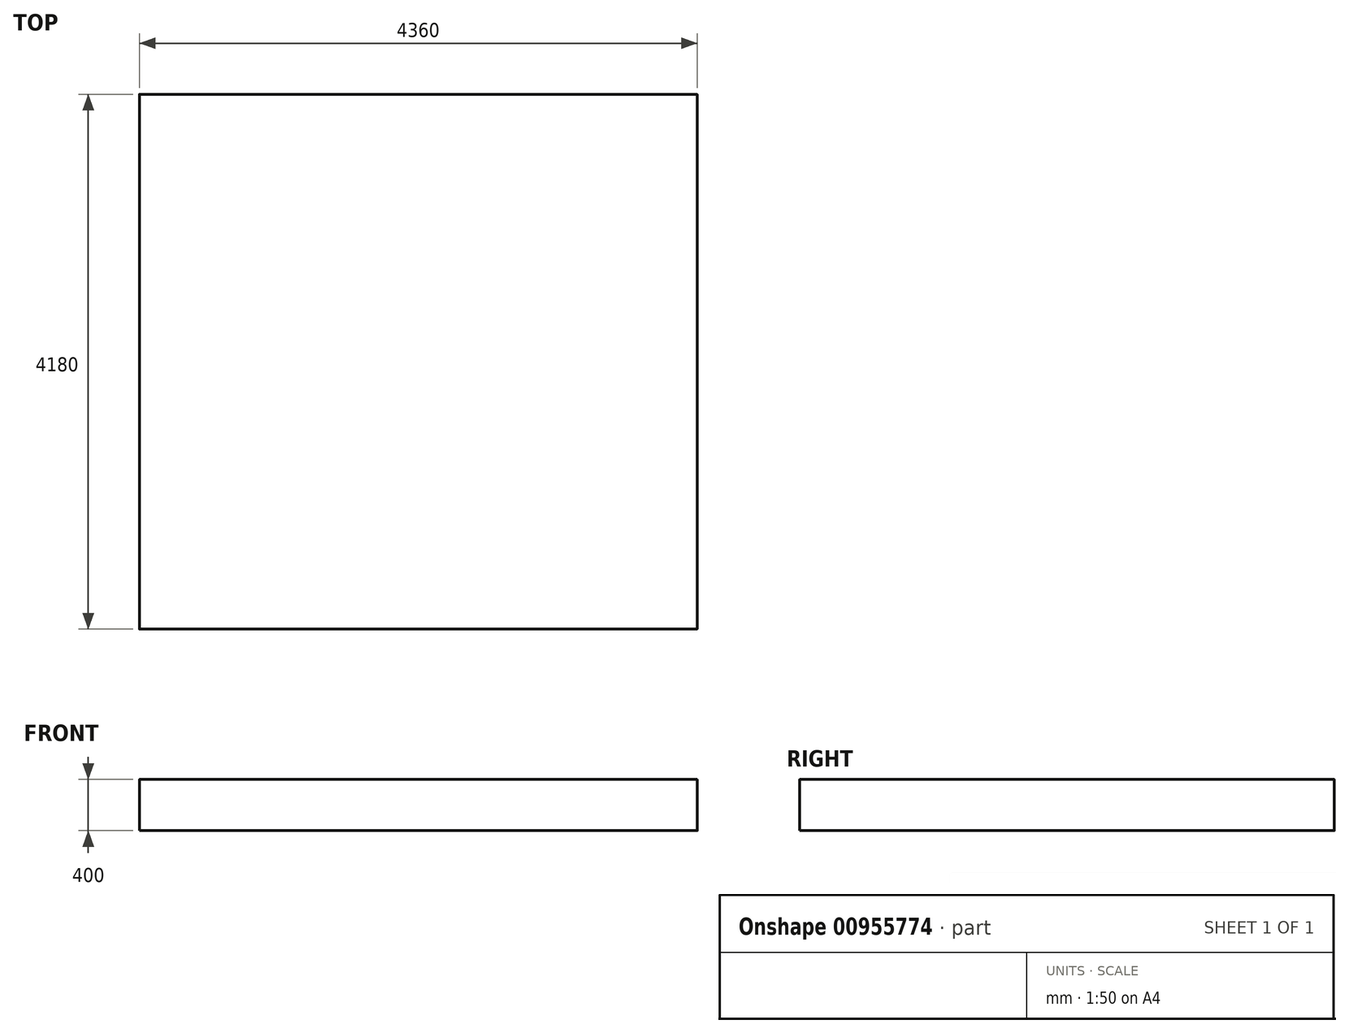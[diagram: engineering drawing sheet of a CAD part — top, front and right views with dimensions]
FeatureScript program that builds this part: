
annotation { "Feature Type Name" : "Feature", "Feature Type Description" : "" }
export const myFeature = defineFeature(function(context is Context, id is Id, definition is map)
    precondition{}
    {
        {
            var Q0;
            Q0=qCreatedBy(makeId("Top.planeOp"),FACE);
            var sketch = newSketch(context, id + "F0", { "sketchPlane" : qUnion([Q0])});
            skLineSegment(sketch, "E0.bottom", {"start": v(-3761.74, 3673.88) * mm, "end": v(598.26, 3673.88) * mm});
            skLineSegment(sketch, "E0.top", {"start": v(-3761.74, -506.12) * mm, "end": v(598.26, -506.12) * mm});
            skLineSegment(sketch, "E0.left", {"start": v(-3761.74, 3673.88) * mm, "end": v(-3761.74, -506.12) * mm});
            skLineSegment(sketch, "E0.right", {"start": v(598.26, 3673.88) * mm, "end": v(598.26, -506.12) * mm});
            skSolve(sketch);
        }
        {
            var Q0;
            Q0 = qSketchRegion(id + "F0", true);
            extrude(context, id + "F1", {"entities" : qUnion([Q0]), "depth" : 400 * mm, "offsetDistance" : 25.4 * mm});
        }
        {
            var Q0;
            Q0=makeQuery(id+"F1.opExtrude","CAP_EDGE",EDGE,{"disambiguationData":[OSD([sQuery(id+"F0.wireOp",EDGE,"E0.bottom")])],"isStart":false});
            fillet(context, id + "F2", {"entities" : qUnion([Q0]), "radius" : ((0.5 * sqrt(2)) / 2) * mm, "tangentPropagation" : true, "allowEdgeOverflow" : false});
        }
        {
            var Q0;
            Q0=makeQuery(id+"F1.opExtrude","CAP_EDGE",EDGE,{"disambiguationData":[OSD([sQuery(id+"F0.wireOp",EDGE,"E0.left")])],"isStart":false});
            fillet(context, id + "F3", {"entities" : qUnion([Q0]), "radius" : ((0.5 * sqrt(2)) / 2) * mm, "tangentPropagation" : true, "allowEdgeOverflow" : false});
        }
        {
            var Q0;
            Q0=makeQuery(id+"F1.opExtrude","CAP_EDGE",EDGE,{"disambiguationData":[OSD([sQuery(id+"F0.wireOp",EDGE,"E0.top")])],"isStart":false});
            fillet(context, id + "F4", {"entities" : qUnion([Q0]), "radius" : ((0.5 * sqrt(2)) / 2) * mm, "tangentPropagation" : true, "allowEdgeOverflow" : false});
        }
        {
            var Q0;
            Q0=makeQuery(id+"F1.opExtrude","CAP_EDGE",EDGE,{"disambiguationData":[OSD([sQuery(id+"F0.wireOp",EDGE,"E0.right")])],"isStart":false});
            fillet(context, id + "F5", {"entities" : qUnion([Q0]), "radius" : ((0.5 * sqrt(2)) / 2) * mm, "tangentPropagation" : true, "allowEdgeOverflow" : false});
        }
    });
